# Revit family: FH-Wall
name_source: partatom
category: Lighting Fixtures
units: mm (PartAtom-declared; Revit-internal decimal feet)

## family parameters
Cut with Voids When Loaded = No
Host = Face
Light Source = No
OmniClass Number = 23.80.70.00
OmniClass Title = Lighting
Part Type = Normal
Room Calculation Point = No
Round Connector Dimension = Use Diameter
Shared = No

## types (2) — shared parameters
Assembly Code = D5020200
Certifications = UL listed
Default Elevation = 48 "
Description = Product Description Flex features AALs exclusive MicroCore technology which provides ample, smooth, even illumination of the environment. The precision aiming system of AALs MicroCore technology ensures that even when looking directly at the luminaire, only one-half of the LEDs can be viewed at any given time. Upgrade kits are available for existing HID installations. Multiple arm designs and mounting options, including single, twin, tri and quad shape, form a versatile create it yourself look.
Dimming Interface = 0-10V
Extension = Yes
Features = Reliable, uniform, glare free illumination
Types II, III, IV, V and custom distributions
3000K, 4000K, 5000K CCT
0-10V dimming ready
Integral surge suppression
LifeShieldTM thermal protection
DLC QPL pending
14 standard powder coat finishes
Upgrade Kits
Glass = Paint - Matte White
Housing = Metal-Galvanized_Steel
IP Rating = IP 66
Lamp = LED
Manufacturer = Architectural Area Lighting
Model = FH
Pole Finish = Metal-Aluminum Alloy
Power Factor = 0.90
Type Comments = Light Fixture
URL = https://www.currentlighting.com
Warranty = 5 Years Limited Warranty
Width = 8.85 "

## per-type parameters (varying)
| type | Curved Arm | Curved Arm with Extension | Straight Arm | Straight Arm With Extension |
| FH-Straight-Arm | No | No | Yes | Yes |
| FH-Curved-Arm | Yes | Yes | No | No |

## geometry (parser evidence)
native form markers: Blend x4, Sweep x7
no freeform markers — native parametric forms only
